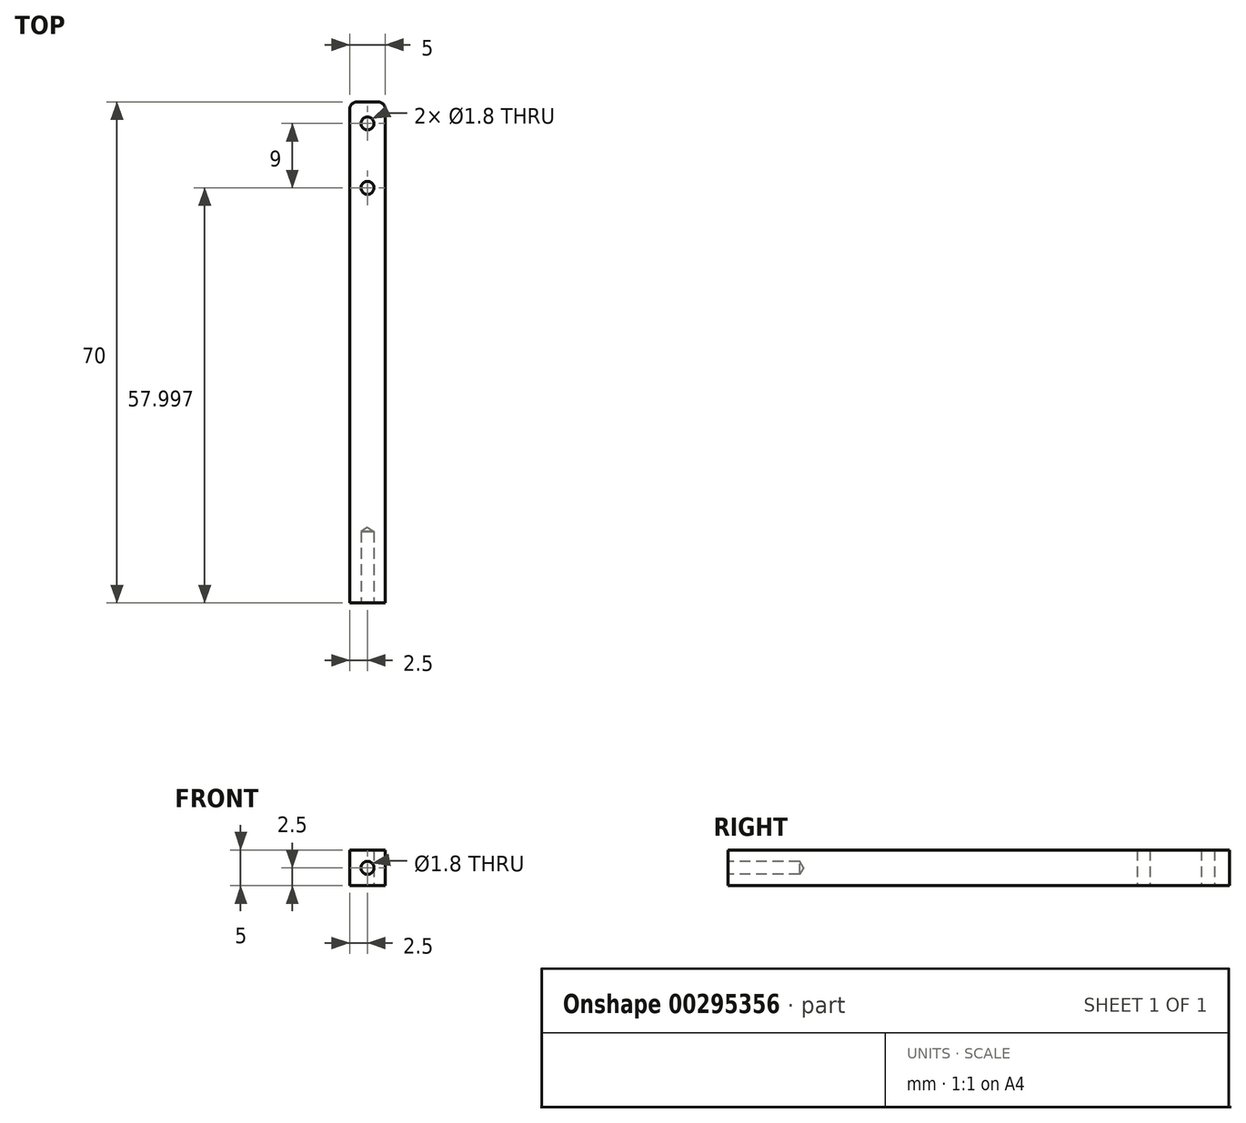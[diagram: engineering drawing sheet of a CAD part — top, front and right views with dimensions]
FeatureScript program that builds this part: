
annotation { "Feature Type Name" : "Feature", "Feature Type Description" : "" }
export const myFeature = defineFeature(function(context is Context, id is Id, definition is map)
    precondition{}
    {
        {
            var Q0;
            Q0=qCreatedBy(makeId("Top.planeOp"),FACE);
            var sketch = newSketch(context, id + "F0", { "sketchPlane" : qUnion([Q0])});
            skLineSegment(sketch, "E0.top", {"start": v(1.5, 22.73) * mm, "end": v(-1.5, 22.73) * mm});
            skLineSegment(sketch, "E0.left", {"start": v(2.5, -47.27) * mm, "end": v(2.5, 21.73) * mm});
            skLineSegment(sketch, "E0.right", {"start": v(-2.5, -47.27) * mm, "end": v(-2.5, 21.73) * mm});
            skPoint(sketch, "E0.middle", {"position": v(0, 0) * mm});
            skCircle(sketch, "E1", {"center": v(0, 19.73) * mm, "radius": 0.9 * mm});
            skCircle(sketch, "E2", {"center": v(0, 10.73) * mm, "radius": 0.9 * mm});
            skPoint(sketch, "E3", {"position": v(0, 26.73) * mm});
            skPoint(sketch, "E4", {"position": v(0, 36.73) * mm});
            skPoint(sketch, "E5.visualSharp", {"position": v(-2.5, 22.73) * mm});
            skArc(sketch, "E5.filletArc", {"start": v(-1.5, 22.73) * mm, "mid": v(-2.2, 22.43) * mm, "end": v(-2.5, 21.73) * mm});
            skPoint(sketch, "E6.visualSharp", {"position": v(2.5, 22.73) * mm});
            skArc(sketch, "E6.filletArc", {"start": v(2.5, 21.73) * mm, "mid": v(2.2, 22.43) * mm, "end": v(1.5, 22.73) * mm});
            skLineSegment(sketch, "E7", {"start": v(-2.5, -47.27) * mm, "end": v(2.5, -47.27) * mm});
            skPoint(sketch, "E8", {"position": v(0, -53.27) * mm});
            skSolve(sketch);
        }
        {
            var Q0;
            Q0=makeQuery(id+"F0.imprint","IMPRINT",FACE,{"disambiguationData":[TD([[makeQuery(id+"F0.imprint","IMPRINT",EDGE,{"derivedFrom":sQuery(id+"F0.wireOp",EDGE,"E0.top")}),1.0]])]});
            extrude(context, id + "F1", {"entities" : qUnion([Q0]), "depth" : 5 * mm});
        }
        {
            var Q0;
            Q0=makeQuery(id+"F1.opExtrude","SWEPT_FACE",FACE,{"disambiguationData":[OSD([sQuery(id+"F0.wireOp",EDGE,"E7")])]});
            var sketch = newSketch(context, id + "F2", { "sketchPlane" : qUnion([Q0])});
            skCircle(sketch, "E9", {"center": v(0, 2.5) * mm, "radius": 5.5 * mm});
            skSolve(sketch);
        }
        {
            var Q0;
            Q0=sQuery(id+"F2.wireOp",VERTEX,"E9.center");
            var Q1;
            Q1=makeQuery(id+"F1.opExtrude","SWEPT_BODY",BODY,{"disambiguationData":[OSD([sQuery(id+"F0.wireOp",EDGE,"E0.top"),sQuery(id+"F0.wireOp",EDGE,"E0.left"),sQuery(id+"F0.wireOp",EDGE,"E0.right"),sQuery(id+"F0.wireOp",EDGE,"E1"),sQuery(id+"F0.wireOp",EDGE,"E2"),sQuery(id+"F0.wireOp",EDGE,"E5.filletArc"),sQuery(id+"F0.wireOp",EDGE,"E6.filletArc"),sQuery(id+"F0.wireOp",EDGE,"E7")])]});
            hole(context, id + "F3", {"style" : HoleStyle.SIMPLE, "endStyle" : HoleEndStyle.BLIND, "holeDiameter" : 1.8 * mm, "holeDepth" : 10 * mm, "tappedDepth" : 12 * mm, "tapClearance" : 3, "locations" : qUnion([Q0]), "scope" : qUnion([Q1])});
        }
    });
